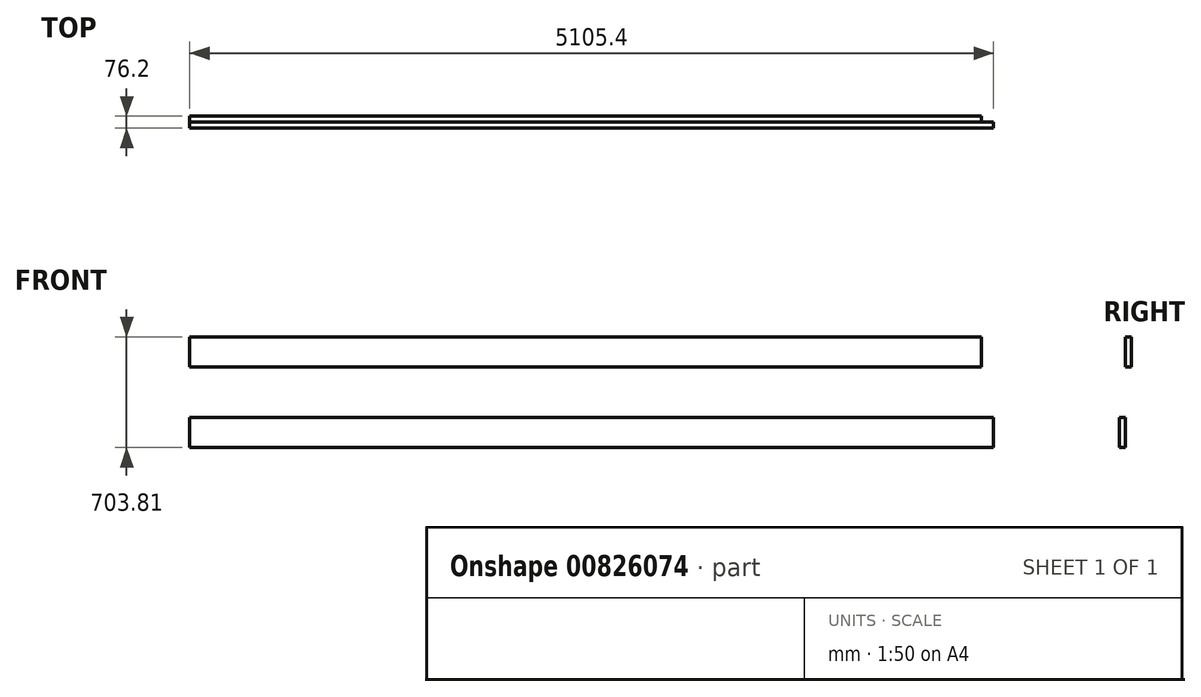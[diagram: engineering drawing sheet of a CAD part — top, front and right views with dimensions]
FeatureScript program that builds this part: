
annotation { "Feature Type Name" : "Feature", "Feature Type Description" : "" }
export const myFeature = defineFeature(function(context is Context, id is Id, definition is map)
    precondition{}
    {
        {
            var Q0;
            Q0=qCreatedBy(makeId("Front.planeOp"),FACE);
            var sketch = newSketch(context, id + "F0", { "sketchPlane" : qUnion([Q0])});
            skLineSegment(sketch, "E0.bottom", {"start": v(0, 0) * mm, "end": v(5105.4, 0) * mm});
            skLineSegment(sketch, "E0.top", {"start": v(0, 190.5) * mm, "end": v(5105.4, 190.5) * mm});
            skLineSegment(sketch, "E0.left", {"start": v(0, 0) * mm, "end": v(0, 190.5) * mm});
            skLineSegment(sketch, "E0.right", {"start": v(5105.4, 0) * mm, "end": v(5105.4, 190.5) * mm});
            skSolve(sketch);
        }
        {
            var Q0;
            Q0=qSketchRegion(id+"F0",true);
            extrude(context, id + "F1", {"entities" : qUnion([Q0]), "depth" : 38.1 * mm, "offsetDistance" : 25.4 * mm});
        }
        {
            var Q0;
            Q0=qCreatedBy(makeId("Right.planeOp"),FACE);
            var sketch = newSketch(context, id + "F2", { "sketchPlane" : qUnion([Q0])});
            skLineSegment(sketch, "E1.bottom", {"start": v(0, 513.31) * mm, "end": v(38.1, 513.31) * mm});
            skLineSegment(sketch, "E1.top", {"start": v(0, 703.81) * mm, "end": v(38.1, 703.81) * mm});
            skLineSegment(sketch, "E1.left", {"start": v(0, 513.31) * mm, "end": v(0, 703.81) * mm});
            skLineSegment(sketch, "E1.right", {"start": v(38.1, 513.31) * mm, "end": v(38.1, 703.81) * mm});
            skSolve(sketch);
        }
        {
            var Q0;
            Q0=qSketchRegion(id+"F2",true);
            extrude(context, id + "F3", {"entities" : qUnion([Q0]), "depth" : 5029.2 * mm, "offsetDistance" : 25.4 * mm});
        }
    });
